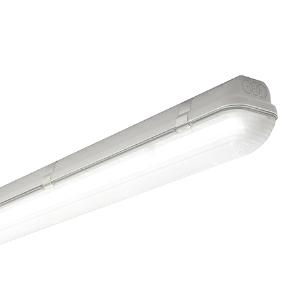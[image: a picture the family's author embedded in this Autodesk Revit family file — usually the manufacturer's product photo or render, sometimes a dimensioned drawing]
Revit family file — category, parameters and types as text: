
# Revit family: 3f_filippi_-_3f_linda_soft_3f_filippi_-_58736_-_3f_linda_led_soft_1x30w_dali_l1570
name_source: partatom
category: Lighting Fixtures
units: mm (PartAtom-declared; Revit-internal decimal feet)

## family parameters
Cut with Voids When Loaded = No
Host = Face
Light Source = No
Part Type = Normal
Room Calculation Point = No
Round Connector Dimension = Use Diameter
Shared = No

## types (1)
- 3F Filippi - 3F Linda Soft (1 x LED, 4755 lm, 33.5 W, 4000 K)
    Apparent Load = 34 VA
    Approval mark = CE
    CIE Flux Codes = 39 68 88 89 100
    Color Rendering = 80
    Color Temperature = 4000 K
    Control Gear = Electronic transformer
    Default Elevation = 1800 mm
    Description = ILLUMINOTECHNICAL
Luminous efficiency 100% (DLOR 89%, ULOR 11%).
Initial luminous flux of the luminaire 4755 lm.
Direct symmetric distribution.
Installation Interdistance Transv.D = 1.39 x hu - Long.D = 1.21 x hu.
Tabular UGR (CIE 117 - 4H-8H; S=0.25H; 70/50/20): RUG 24 - 21.
Beam angle: 149° - 108°.
Luminous efficacy 142 lm/W.
Lifetime (L93/B10): 30000 h. (tq+25°C)
Lifetime (L90/B10): 50000 h. (tq+25°C)
Lifetime (L85/B10): 80000 h. (tq+25°C)
Lifetime (L80/B10): 100000 h. (tq+25°C)
Lifetime (L85/B10): 50000 h. (tq+35°C)
Sudden decreased luminous flux after 50000 hours: 0% (C0).
Photobiological safety in compliance with IEC/TR 62778: RG0 risk exempt, (IEC 62471).
In compliance with IEC/EN 62722-2-1 - IEC/EN 62717 standards.

SOURCE
Linear LED module 30W/840.
Energy efficiency class (UE 2019/2020 - UE 2019/2015): D.
CIE 13.3 Colour rendering index: CRI >80 (R9 <50%).
IES TM-30 Fidelity Index: Rf = 84 Rg = 95.
CCT nominal colour temperature 4000 K.
Colour initial tolerance (MacAdam): SDCM 3.

MECHANICAL
Self-extinguishing V2 polycarbonate housing, injection moulded, RAL 7035 grey.
Ecologic anti-aging injected sealing gasket.
Soft opal diffuser in self-extinguishing V2 polycarbonate, photo-engraved interior, UV stabilised, injection moulded.
Gear-holder reflector in hot-dip galvanised steel, painted with white polyester base.
Snug fit safety snap-lock clips for diffuser mounting in stainless steel, screwdriver opening.
Fixing brackets in stainless steel.
Possibility for technicians to access the interior of the luminaire.
Luminaire with limited surface temperature. - D - (EN 60598-2-24)
Dimensions: 1570x100 mm, height 100 mm. Weight 2.52 kg.
IP66 protection degree.
Mechanical strength to impacts IK10 (20 joule).
Glow-wire test resistance 850°C.

ELECTRICAL
Halogen Free DALI-2 DATI (Parts 251, 252, 253), PUSH-DIM, electronic wiring 230V-50/60Hz, power factor 0.95 at full load, THD <25%, constant output current, SELV, class I, 1 driver, 1 DALI addresse.
Power of the luminaire 33.5 W.
ENEC - CE.
SAFE FLICKER: PstLM=<1 and SVM=<0.4 (IEC TR 61547-1 and IEC TR 63158), to ensure a more comfortable and safe light.
Luminaire compliant with EN 60598-2-22 for power supply from a centralised emergency system CPSS (Central Power Supply System), not incorporated in the luminaire - high risk areas excluded. The default power and flux are 100% in AC and 15% in DC.
Ambient temperature from -20°C to +35°C.
Temperature class T6 max 85°C.
Relative humidity UR: <85%.

INSTALLATION
Ceiling / Suspended / Wall.
All accessories dedicated to this product are available on the Catalog and on our website www.3F-Filippi.com.

APPLICATIONS
Suitable product for food production plants (HACCP), IFS (Food Version 6), BRC (GSFS Food Version 7).
Dry, dusty indoor environments, subject to occasional water splashes.
Luminaires designed for diffuse direct/indirect lighting suitable to provide optimum visual comfort.
Transit areas, stairwells.
Virtually shatterproof polycarbonate compatibly with the fumes / atmospheres that compromise the elasticity of plastic materials.
Suitable for illumination of public car parks and parking grounds referred to DIN 67528:2018-04.

LIGHT MANAGEMENT
Recommended minimum setting: 10%.
The luminaire, equipped with (DALI-2 DATI) driver, can be controlled manually with 3F Easy Dim technology or automatically/manually with wired or wireless DALI/D2D control systems.
The D2D driver guarantees interoperability with other devices with the same certification by making the following information available:
Device Data (Part 251), Energy Report (Part 252), Diagnosis & Maintenance (Part 253).
In electrical systems without a regulation system (manual or automatic) and DALI bus, a suitable jumper must be made on the DA-DA terminals of the appliance.

WARNING
Fixture not suitable for cold stores with an ambient temperature <0°C and/or relative humidity >85%.
Luminaire designed for disposal/recycling at end-of-life.
Replaceable (LED only) light source by a professional. Replaceable control gear by a professional.
    Height = 100 mm  [stored 0.328084 ft]
    Lamp = 1 x LED
    Lamp Light Flux = 4755 lm
    Lamp Power = 33.5 W
    Lamp count = 1
    Length = 1570 mm
    Lifetime = 50000 h
    Luminous efficacy = 142 lm/W
    Manufacturer = 3F Filippi
    ModVariant = No
    Model = 3F Filippi - 58736 - 3F Linda LED Soft 1x30W DALI L1570
    Mounting Place = Ceiling
    Mounting Type = Pendant
    Number of Poles = 1
    OnlyDefault = Yes
    Power Factor = 1
    Product Name = 3F Filippi - 3F Linda Soft
    Product group = pendant luminaire
    ProductGroupID = 9
    Protection Class = Protection class I
    Protection Degree = IP 66
    RLX_Detail_Level = 1
    RLX_Emergency_Light_Flux = 0 lm
    RLX_Emergency_Type = 0
    RLX_Emergency_Type_DB = No
    RlxData = <blob elided: 61905 chars, md5=155d0609>
    Socket = socket
    Standby Power = 0 W
    System Light Flux = 4755 lm
    System Power = 34 W
    Type Comments = Product without accessories
    Type Image = 3ffilippi_3f_linda_led_soft_1x.jpg
    URL = http://relux.com
    VarID = ---
    Voltage = 0 V
    Weight = 0.00 kg
    Width = 100 mm  [stored 0.328084 ft]

note: [stored X ft] marks values corroborated as IEEE doubles in the binary element streams (Revit-internal decimal feet)

## geometry (parser evidence)
native form markers: Blend x4, Sweep x12
no freeform markers — native parametric forms only
